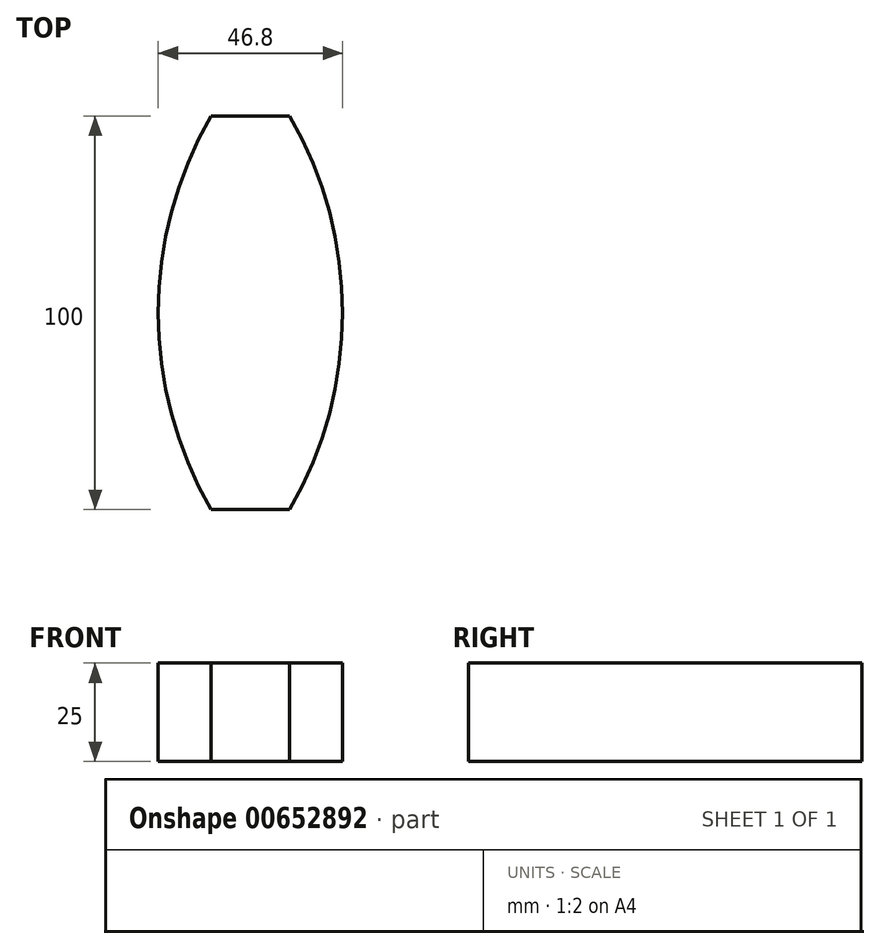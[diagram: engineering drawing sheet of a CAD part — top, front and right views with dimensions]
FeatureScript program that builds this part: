
annotation { "Feature Type Name" : "Feature", "Feature Type Description" : "" }
export const myFeature = defineFeature(function(context is Context, id is Id, definition is map)
    precondition{}
    {
        {
            var Q0;
            Q0=qCreatedBy(makeId("Top.planeOp"),FACE);
            var sketch = newSketch(context, id + "F0", { "sketchPlane" : qUnion([Q0])});
            skLineSegment(sketch, "E0.bottom", {"start": v(10, -50) * mm, "end": v(-10, -50) * mm, "construction": true});
            skLineSegment(sketch, "E0.top", {"start": v(10, 50) * mm, "end": v(-10, 50) * mm, "construction": true});
            skLineSegment(sketch, "E0.left", {"start": v(10, -50) * mm, "end": v(10, 50) * mm, "construction": true});
            skLineSegment(sketch, "E0.right", {"start": v(-10, -50) * mm, "end": v(-10, 50) * mm, "construction": true});
            skPoint(sketch, "E0.middle", {"position": v(0, 0) * mm});
            skArc(sketch, "E1", {"start": v(-10, 50) * mm, "mid": v(-23.4, 0) * mm, "end": v(-10, -50) * mm});
            skArc(sketch, "E2.MirrorCS", {"start": v(10, 50) * mm, "mid": v(23.4, 0) * mm, "end": v(10, -50) * mm});
            skLineSegment(sketch, "E3", {"start": v(-10, 50) * mm, "end": v(10, 50) * mm});
            skLineSegment(sketch, "E4", {"start": v(-10, -50) * mm, "end": v(10, -50) * mm});
            skSolve(sketch);
        }
        {
            var Q0;
            Q0=makeQuery(id+"F0.imprint","IMPRINT",FACE,{"disambiguationData":[TD([[makeQuery(id+"F0.imprint","IMPRINT",EDGE,{"derivedFrom":sQuery(id+"F0.wireOp",EDGE,"E1")}),1.0]])]});
            extrude(context, id + "F1", {"entities" : qUnion([Q0]), "depth" : 25 * mm, "offsetDistance" : 25 * mm});
        }
    });
